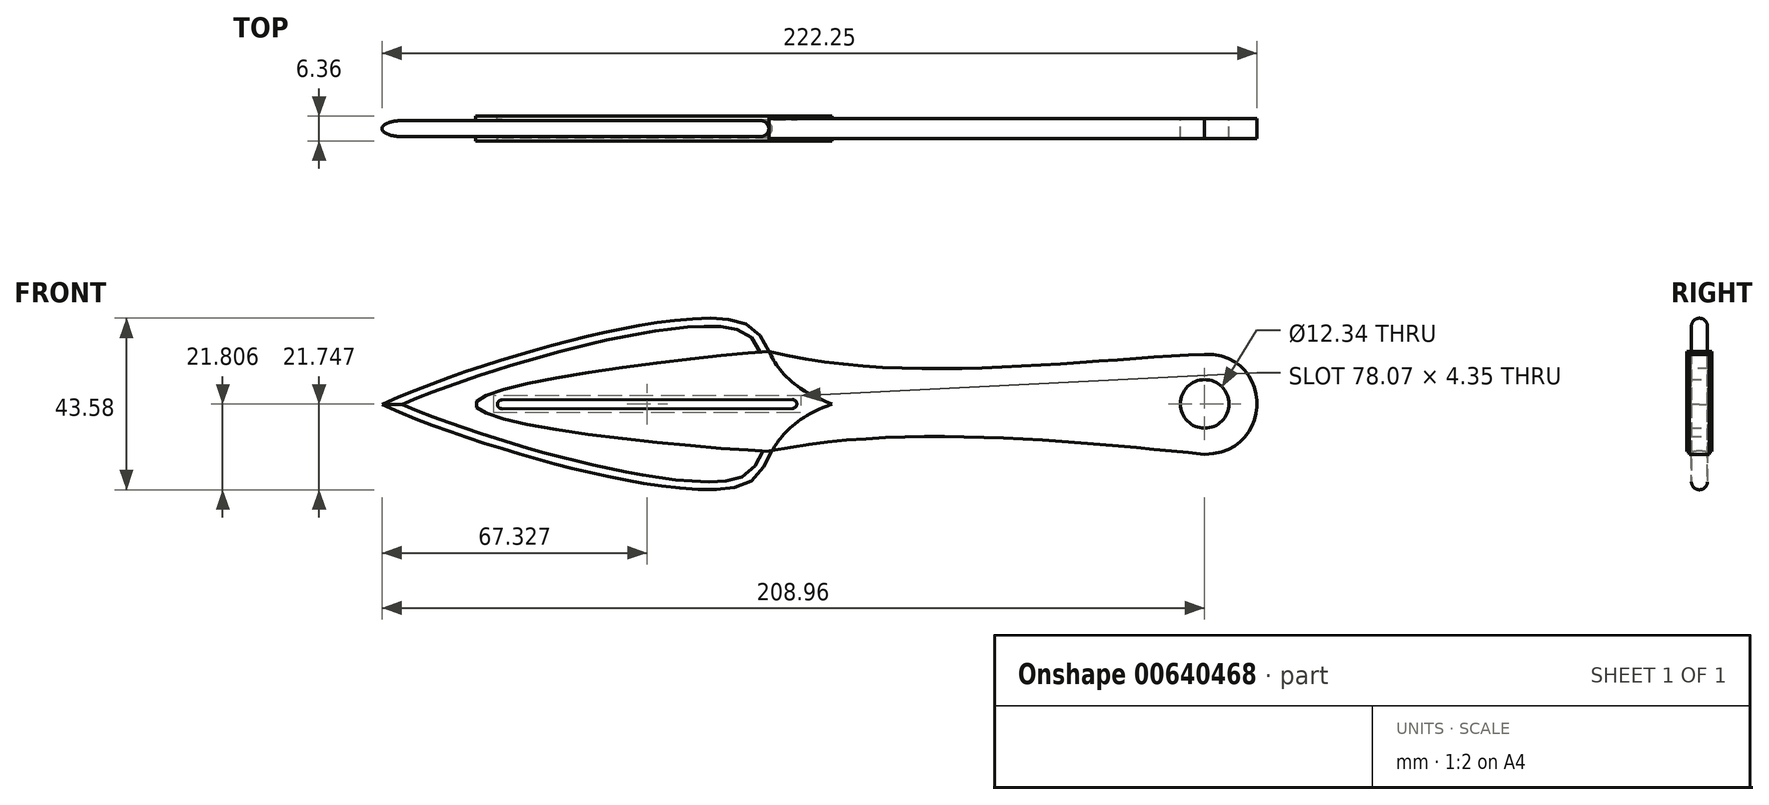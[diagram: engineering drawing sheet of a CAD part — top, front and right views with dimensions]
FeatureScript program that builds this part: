
annotation { "Feature Type Name" : "Feature", "Feature Type Description" : "" }
export const myFeature = defineFeature(function(context is Context, id is Id, definition is map)
    precondition{}
    {
        {
            var Q0;
            Q0=qCreatedBy(makeId("Front.planeOp"),FACE);
            var sketch = newSketch(context, id + "F0", { "sketchPlane" : qUnion([Q0])});
            skFitSpline(sketch, "E0", {"points": [v(-98.23, 23.1) * mm, v(-6, 43.65) * mm, v(16.07, 23.25) * mm], "startDerivative": vector(115.3, 53.4) * mm, "endDerivative": vector(155.68, -56.97) * mm});
            skFitSpline(sketch, "E1", {"points": [v(0, 36.61) * mm, v(110.73, 35.86) * mm], "startDerivative": vector(104.99, -26.21) * mm, "endDerivative": vector(94.67, 3.9) * mm});
            skFitSpline(sketch, "E2", {"points": [v(0, 11.21) * mm, v(110.73, 10.46) * mm], "startDerivative": vector(104.97, 21.73) * mm, "endDerivative": vector(94.67, -9.08) * mm});
            skFitSpline(sketch, "E3", {"points": [v(110.73, 10.46) * mm, v(110.73, 35.86) * mm], "startDerivative": vector(53.16, 0.6) * mm, "endDerivative": vector(-53.16, -0.6) * mm});
            skFitSpline(sketch, "E4", {"points": [v(0, 36.61) * mm, v(-74.53, 23.13) * mm, v(0, 11.21) * mm], "startDerivative": vector(-103.22, -7.9) * mm, "endDerivative": vector(103.4, -4.12) * mm});
            skFitSpline(sketch, "E5", {"points": [v(-98.23, 23.1) * mm, v(-6, 2.8) * mm, v(16.07, 23.25) * mm], "startDerivative": vector(115.34, -53.1) * mm, "endDerivative": vector(155.6, 58.86) * mm});
            skCircle(sketch, "E6", {"center": v(110.73, 23.25) * mm, "radius": 6.17 * mm});
            skLineSegment(sketch, "E7", {"start": v(-67.8, 24.26) * mm, "end": v(6, 24.35) * mm});
            skLineSegment(sketch, "E8", {"start": v(-67.8, 22.02) * mm, "end": v(6, 22.12) * mm});
            skArc(sketch, "E9", {"start": v(-67.8, 24.26) * mm, "mid": v(-68.93, 23.14) * mm, "end": v(-67.8, 22.02) * mm});
            skArc(sketch, "E10", {"start": v(6, 22.12) * mm, "mid": v(7.12, 23.24) * mm, "end": v(6, 24.35) * mm});
            skPoint(sketch, "E11", {"position": v(124.02, 23.25) * mm});
            skPoint(sketch, "E12", {"position": v(-129.6, -34.32) * mm});
            skSolve(sketch);
        }
        {
            var Q0;
            {var subQ0=sQuery(id+"F0.wireOp",EDGE,"Vf1Qqvtc-29Q4-ATyL-Uykj-3RGwVTXjJFBV");var subQ3=sQuery(id+"F0.wireOp",EDGE,"E4");var subQ5=makeQuery(id+"F0.imprint","INTERSECT",VERTEX,{"derivedFrom":[subQ0,subQ3]});Q0=makeQuery(id+"F0.imprint","IMPRINT",FACE,{"disambiguationData":[TD([[makeQuery(id+"F0.imprint","IMPRINT",EDGE,{"disambiguationData":[TD([[subQ5,-1.0]])],"derivedFrom":subQ0}),1.0]])]});}
            var Q1;
            {var subQ3=sQuery(id+"F0.wireOp",EDGE,"E2");var subQ5=sQuery(id+"F0.wireOp",EDGE,"E4");var subQ6=makeQuery(id+"F0.imprint","INTERSECT",VERTEX,{"derivedFrom":[subQ3,subQ5]});Q1=makeQuery(id+"F0.imprint","IMPRINT",FACE,{"disambiguationData":[TD([[makeQuery(id+"F0.imprint","IMPRINT",EDGE,{"disambiguationData":[TD([[subQ6,-1.0]])],"derivedFrom":subQ3}),1.0]])]});}
            extrude(context, id + "F1", {"entities" : qUnion([Q0, Q1]), "endBound" : BoundingType.SYMMETRIC, "depth" : 6.35 * mm, "offsetDistance" : 25.4 * mm});
        }
        {
            var Q0;
            {var subQ0=sQuery(id+"F0.wireOp",EDGE,"E1");Q0=makeQuery(id+"F0.imprint","IMPRINT",FACE,{"disambiguationData":[TD([[makeQuery(id+"F0.imprint","IMPRINT",EDGE,{"derivedFrom":subQ0}),-1.0]])]});}
            extrude(context, id + "F2", {"entities" : qUnion([Q0]), "endBound" : BoundingType.SYMMETRIC, "depth" : 5.08 * mm, "offsetDistance" : 25.4 * mm});
        }
        {
            var Q0;
            {var subQ0=sQuery(id+"F0.wireOp",EDGE,"Vf1Qqvtc-29Q4-ATyL-Uykj-3RGwVTXjJFBV");var subQ3=sQuery(id+"F0.wireOp",EDGE,"E4");var subQ5=makeQuery(id+"F0.imprint","INTERSECT",VERTEX,{"derivedFrom":[subQ0,subQ3]});Q0=makeQuery(id+"F0.imprint","IMPRINT",FACE,{"disambiguationData":[TD([[makeQuery(id+"F0.imprint","IMPRINT",EDGE,{"disambiguationData":[TD([[subQ5,1.0]])],"derivedFrom":subQ0}),1.0]])]});}
            var Q1;
            {var subQ3=sQuery(id+"F0.wireOp",EDGE,"E2");var subQ5=sQuery(id+"F0.wireOp",EDGE,"E4");var subQ6=makeQuery(id+"F0.imprint","INTERSECT",VERTEX,{"derivedFrom":[subQ3,subQ5]});Q1=makeQuery(id+"F0.imprint","IMPRINT",FACE,{"disambiguationData":[TD([[makeQuery(id+"F0.imprint","IMPRINT",EDGE,{"disambiguationData":[TD([[subQ6,-1.0]])],"derivedFrom":subQ3}),-1.0]])]});}
            extrude(context, id + "F3", {"entities" : qUnion([Q0, Q1]), "operationType" : NewBodyOperationType.ADD, "endBound" : BoundingType.SYMMETRIC, "depth" : 4.06 * mm, "offsetDistance" : 25.4 * mm});
        }
        {
            var Q0;
            Q0=makeQuery(id+"F3.opExtrude","CAP_EDGE",EDGE,{"disambiguationData":[OSD([sQuery(id+"F0.wireOp",EDGE,"E0")])],"isStart":false});
            var Q1;
            Q1=makeQuery(id+"F3.opExtrude","CAP_EDGE",EDGE,{"disambiguationData":[OSD([sQuery(id+"F0.wireOp",EDGE,"E5")])],"isStart":false});
            var Q2;
            Q2=makeQuery(id+"F3.opExtrude","CAP_EDGE",EDGE,{"disambiguationData":[OSD([sQuery(id+"F0.wireOp",EDGE,"E0")])],"isStart":true});
            var Q3;
            Q3=makeQuery(id+"F3.opExtrude","CAP_EDGE",EDGE,{"disambiguationData":[OSD([sQuery(id+"F0.wireOp",EDGE,"E5")])],"isStart":true});
            fillet(context, id + "F4", {"entities" : qUnion([Q0, Q1, Q2, Q3]), "radius" : 2.03 * mm, "tangentPropagation" : true, "allowEdgeOverflow" : false});
        }
        {
            var Q0;
            Q0=makeQuery(id+"F0.imprint","IMPRINT",FACE,{"disambiguationData":[TD([[makeQuery(id+"F0.imprint","IMPRINT",EDGE,{"derivedFrom":sQuery(id+"F0.wireOp",EDGE,"E7")}),-1.0]])]});
            extrude(context, id + "F5", {"entities" : qUnion([Q0]), "operationType" : NewBodyOperationType.ADD, "endBound" : BoundingType.SYMMETRIC, "depth" : 4.57 * mm, "offsetDistance" : 25.4 * mm});
        }
        {
            var Q0;
            Q0=makeQuery(id+"F1.opExtrude","CAP_EDGE",EDGE,{"disambiguationData":[OSD([sQuery(id+"F0.wireOp",EDGE,"E7")])],"isStart":false});
            var Q1;
            Q1=makeQuery(id+"F1.opExtrude","CAP_EDGE",EDGE,{"disambiguationData":[OSD([sQuery(id+"F0.wireOp",EDGE,"E8")])],"isStart":false});
            var Q2;
            Q2=makeQuery(id+"F1.opExtrude","CAP_EDGE",EDGE,{"disambiguationData":[OSD([sQuery(id+"F0.wireOp",EDGE,"E10")])],"isStart":false});
            var Q3;
            Q3=makeQuery(id+"F1.opExtrude","CAP_EDGE",EDGE,{"disambiguationData":[OSD([sQuery(id+"F0.wireOp",EDGE,"E9")])],"isStart":false});
            var Q4;
            Q4=makeQuery(id+"F1.opExtrude","CAP_EDGE",EDGE,{"disambiguationData":[OSD([sQuery(id+"F0.wireOp",EDGE,"E7")])],"isStart":true});
            var Q5;
            Q5=makeQuery(id+"F1.opExtrude","CAP_EDGE",EDGE,{"disambiguationData":[OSD([sQuery(id+"F0.wireOp",EDGE,"E9")])],"isStart":true});
            var Q6;
            Q6=makeQuery(id+"F1.opExtrude","CAP_EDGE",EDGE,{"disambiguationData":[OSD([sQuery(id+"F0.wireOp",EDGE,"E8")])],"isStart":true});
            var Q7;
            Q7=makeQuery(id+"F1.opExtrude","CAP_EDGE",EDGE,{"disambiguationData":[OSD([sQuery(id+"F0.wireOp",EDGE,"E10")])],"isStart":true});
            fillet(context, id + "F6", {"entities" : qUnion([Q0, Q1, Q2, Q3, Q4, Q5, Q6, Q7]), "radius" : 1.02 * mm, "tangentPropagation" : true, "allowEdgeOverflow" : false});
        }
    });
